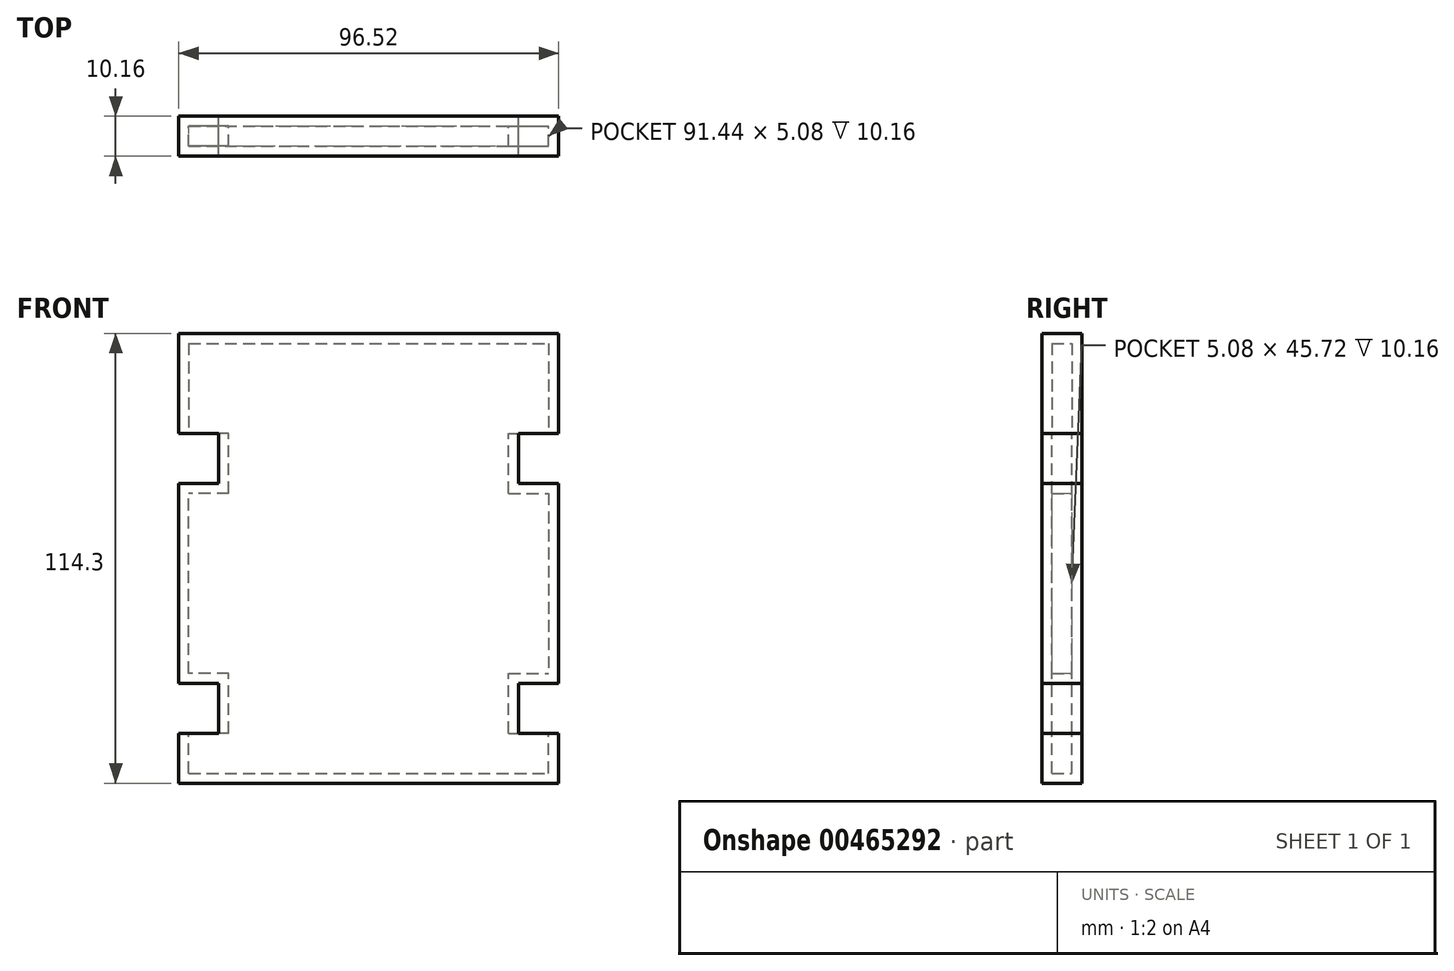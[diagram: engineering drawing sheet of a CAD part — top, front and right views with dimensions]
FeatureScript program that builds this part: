
annotation { "Feature Type Name" : "Feature", "Feature Type Description" : "" }
export const myFeature = defineFeature(function(context is Context, id is Id, definition is map)
    precondition{}
    {
        {
            var Q0;
            Q0=qCreatedBy(makeId("Front.planeOp"),FACE);
            var sketch = newSketch(context, id + "F0", { "sketchPlane" : qUnion([Q0])});
            skLineSegment(sketch, "E0.bottom", {"start": v(38.1, -57.15) * mm, "end": v(-38.1, -57.15) * mm});
            skLineSegment(sketch, "E0.top", {"start": v(38.1, 57.15) * mm, "end": v(-38.1, 57.15) * mm});
            skLineSegment(sketch, "E0.left", {"start": v(38.1, -57.15) * mm, "end": v(38.1, 57.15) * mm});
            skLineSegment(sketch, "E0.right", {"start": v(-38.1, -57.15) * mm, "end": v(-38.1, 57.15) * mm});
            skPoint(sketch, "E0.middle", {"position": v(0, 0) * mm});
            skLineSegment(sketch, "E1.bottom", {"start": v(-38.1, -57.15) * mm, "end": v(-48.26, -57.15) * mm});
            skLineSegment(sketch, "E1.top", {"start": v(-38.1, -44.45) * mm, "end": v(-48.26, -44.45) * mm});
            skLineSegment(sketch, "E1.left", {"start": v(-38.1, -57.15) * mm, "end": v(-38.1, -44.45) * mm});
            skLineSegment(sketch, "E1.right", {"start": v(-48.26, -57.15) * mm, "end": v(-48.26, -44.45) * mm});
            skLineSegment(sketch, "E2.bottom", {"start": v(-38.1, -31.75) * mm, "end": v(-48.26, -31.75) * mm});
            skLineSegment(sketch, "E2.top", {"start": v(-38.1, 19.05) * mm, "end": v(-48.26, 19.05) * mm});
            skLineSegment(sketch, "E2.left", {"start": v(-38.1, -31.75) * mm, "end": v(-38.1, 19.05) * mm});
            skLineSegment(sketch, "E2.right", {"start": v(-48.26, -31.75) * mm, "end": v(-48.26, 19.05) * mm});
            skLineSegment(sketch, "E3.bottom", {"start": v(-38.1, 57.15) * mm, "end": v(-48.26, 57.15) * mm});
            skLineSegment(sketch, "E3.top", {"start": v(-38.1, 31.75) * mm, "end": v(-48.26, 31.75) * mm});
            skLineSegment(sketch, "E3.left", {"start": v(-38.1, 57.15) * mm, "end": v(-38.1, 31.75) * mm});
            skLineSegment(sketch, "E3.right", {"start": v(-48.26, 57.15) * mm, "end": v(-48.26, 31.75) * mm});
            skLineSegment(sketch, "E4.bottom", {"start": v(38.1, 19.05) * mm, "end": v(48.26, 19.05) * mm});
            skLineSegment(sketch, "E4.top", {"start": v(38.1, -31.75) * mm, "end": v(48.26, -31.75) * mm});
            skLineSegment(sketch, "E4.left", {"start": v(38.1, 19.05) * mm, "end": v(38.1, -31.75) * mm});
            skLineSegment(sketch, "E4.right", {"start": v(48.26, 19.05) * mm, "end": v(48.26, -31.75) * mm});
            skLineSegment(sketch, "E5.bottom", {"start": v(38.1, -57.15) * mm, "end": v(48.26, -57.15) * mm});
            skLineSegment(sketch, "E5.top", {"start": v(38.1, -44.45) * mm, "end": v(48.26, -44.45) * mm});
            skLineSegment(sketch, "E5.left", {"start": v(38.1, -57.15) * mm, "end": v(38.1, -44.45) * mm});
            skLineSegment(sketch, "E5.right", {"start": v(48.26, -57.15) * mm, "end": v(48.26, -44.45) * mm});
            skLineSegment(sketch, "E6.bottom", {"start": v(38.1, 57.15) * mm, "end": v(48.26, 57.15) * mm});
            skLineSegment(sketch, "E6.top", {"start": v(38.1, 31.75) * mm, "end": v(48.26, 31.75) * mm});
            skLineSegment(sketch, "E6.left", {"start": v(38.1, 57.15) * mm, "end": v(38.1, 31.75) * mm});
            skLineSegment(sketch, "E6.right", {"start": v(48.26, 57.15) * mm, "end": v(48.26, 31.75) * mm});
            skSolve(sketch);
        }
        {
            var Q0;
            Q0 = qSketchRegion(id + "F0", true);
            extrude(context, id + "F1", {"entities" : qUnion([Q0]), "endBound" : BoundingType.SYMMETRIC, "depth" : 10.16 * mm});
        }
        {
            var Q0;
            Q0=makeQuery(id+"F1.opExtrude","SWEPT_FACE",FACE,{"disambiguationData":[OSD([sQuery(id+"F0.wireOp",EDGE,"E6.top")])]});
            var Q1;
            Q1=makeQuery(id+"F1.opExtrude","SWEPT_FACE",FACE,{"disambiguationData":[OSD([sQuery(id+"F0.wireOp",EDGE,"E5.top")])]});
            var Q2;
            Q2=makeQuery(id+"F1.opExtrude","SWEPT_FACE",FACE,{"disambiguationData":[OSD([sQuery(id+"F0.wireOp",EDGE,"E1.top")])]});
            var Q3;
            Q3=makeQuery(id+"F1.opExtrude","SWEPT_FACE",FACE,{"disambiguationData":[OSD([sQuery(id+"F0.wireOp",EDGE,"E3.top")])]});
            shell(context, id + "F2", {"entities" : qUnion([Q0, Q1, Q2, Q3]), "thickness" : 2.54 * mm});
        }
    });
